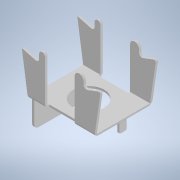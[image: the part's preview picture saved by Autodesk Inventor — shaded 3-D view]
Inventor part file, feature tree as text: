
AUTODESK INVENTOR PART (.ipt)
format: ipt  version: 2021 (Build 250183000, 183)  size: 232,960 bytes
history: native  units: mm
features: other x14, sketch x9, extrude x8, hole x1
ambient origin geometry x8: Origin, YZ Plane, XZ Plane, XY Plane, X Axis, Y Axis, Z Axis, Center Point
bodies: Solid1 (feature_tree)
feature tree (32):
  extrude  "Extrusion1"  Depth=1.4mm TaperAngle=0.0deg
  extrude  "Extrusion2"  Depth=16.7mm TaperAngle=0.0deg
  extrude  "Extrusion3"  Depth=0.7mm TaperAngle=0.0deg
  hole  "Hole1"  [1 undecoded]
  extrude  "Extrusion4"  [1 undecoded]
  extrude  "Extrusion5"  [1 undecoded]
  extrude  "Extrusion6"  [1 undecoded]
  extrude  "Extrusion7"  [1 undecoded]
  extrude  "Extrusion8"  [1 undecoded]
  other  "washer_to_base_XY"
  other  "washer_to_base_YZ"
  other  "washer_to_base_ZX"
  other  "washer_to_base_X"
  other  "washer_to_base_Y"
  other  "washer_to_base_Z"
  other  "washer_to_base_Center"
  other  "washer_to_insert_XY"
  other  "washer_to_insert_YZ"
  other  "washer_to_insert_ZX"
  other  "washer_to_insert_X"
  other  "washer_to_insert_Y"
  other  "washer_to_insert_Z"
  other  "washer_to_insert_Center"
  sketch  "Sketch_1"  dims[d0=29.866667mm d1=0.0mm d2=1.4mm d3=0.0mm]
  sketch  "Sketch_3"  dims[d6=10.5mm d7=6.0mm d8=4.0mm d9=2.0mm d10=90.0deg d11=1.0mm d12=0.0mm d13=16.7mm d14=0.0mm]
  sketch  "Sketch_2"  dims[d4=1.4mm d5=0.0mm]
  sketch  "Sketch4"  dims[d15=19.5mm d16=0.0mm d17=0.7mm d18=0.0mm]
  sketch  "Sketch_5"  dims[d19=2.5mm d20=0.0mm d21=0.78mm d22=0.0mm]
  sketch  "Sketch_9"
  sketch  "Sketch_6"  dims[d23=0.0mm]
  sketch  "Sketch_7"
  sketch  "Sketch_8"
note: 6 required parameter values undecoded (feature->parameter linkage not recoverable at this tier; creation-order binding heuristic only, values carry confidence <= 0.55)
